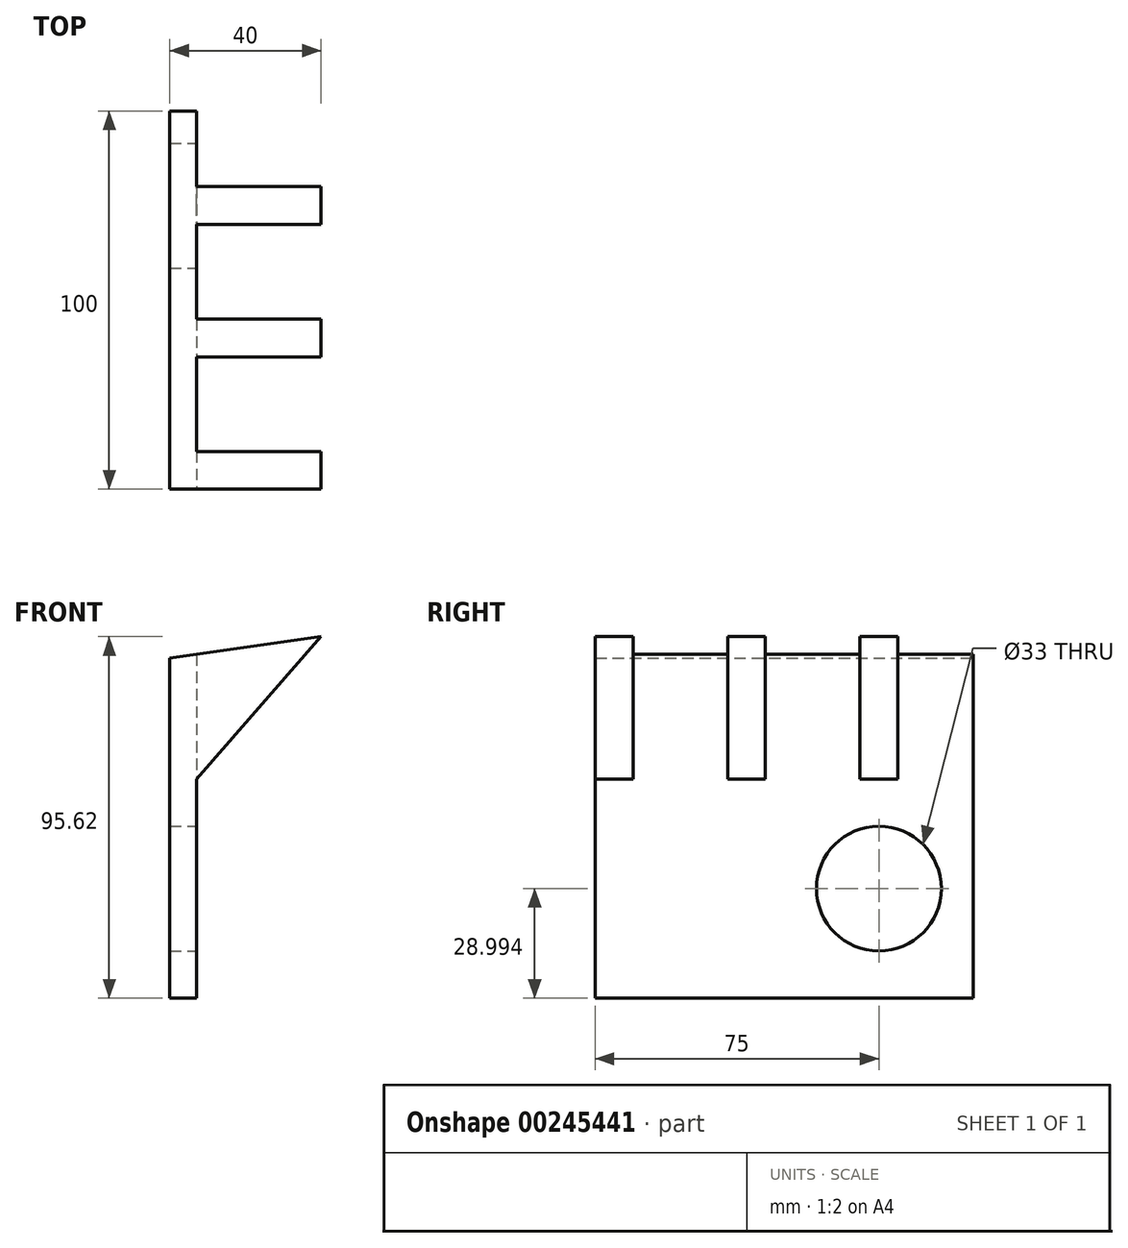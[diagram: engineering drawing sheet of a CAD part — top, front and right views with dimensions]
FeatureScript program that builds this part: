
annotation { "Feature Type Name" : "Feature", "Feature Type Description" : "" }
export const myFeature = defineFeature(function(context is Context, id is Id, definition is map)
    precondition{}
    {
        {
            var Q0;
            Q0=qCreatedBy(makeId("Front.planeOp"),FACE);
            var sketch = newSketch(context, id + "F0", { "sketchPlane" : qUnion([Q0])});
            skLineSegment(sketch, "E0", {"start": v(0, 0) * mm, "end": v(0, 90) * mm});
            skLineSegment(sketch, "E1", {"start": v(0, 90) * mm, "end": v(148.54, 110.88) * mm});
            skLineSegment(sketch, "E2", {"start": v(148.54, 110.88) * mm, "end": v(148.54, 0) * mm});
            skLineSegment(sketch, "E3", {"start": v(148.54, 0) * mm, "end": v(0, 0) * mm});
            skSolve(sketch);
        }
        {
            var Q0;
            Q0=qSketchRegion(id+"F0",true);
            extrude(context, id + "F1", {"entities" : qUnion([Q0]), "depth" : 100 * mm});
        }
        {
            var Q0;
            Q0=makeQuery(id+"F1.opExtrude","CAP_FACE",FACE,{"disambiguationData":[OSD([sQuery(id+"F0.wireOp",EDGE,"E0"),sQuery(id+"F0.wireOp",EDGE,"E1"),sQuery(id+"F0.wireOp",EDGE,"E2"),sQuery(id+"F0.wireOp",EDGE,"E3")])],"isStart":false});
            var sketch = newSketch(context, id + "F2", { "sketchPlane" : qUnion([Q0])});
            skLineSegment(sketch, "E4", {"start": v(0, 0) * mm, "end": v(7, 0) * mm});
            skLineSegment(sketch, "E5.bottom", {"start": v(40, 0) * mm, "end": v(148.54, 0) * mm});
            skLineSegment(sketch, "E5.top", {"start": v(40, 169.22) * mm, "end": v(148.54, 169.22) * mm});
            skLineSegment(sketch, "E5.left", {"start": v(40, 95.62) * mm, "end": v(40, 169.22) * mm});
            skLineSegment(sketch, "E5.right", {"start": v(148.54, 0) * mm, "end": v(148.54, 169.22) * mm});
            skLineSegment(sketch, "E6", {"start": v(40, 95.62) * mm, "end": v(7, 57.99) * mm});
            skLineSegment(sketch, "E7", {"start": v(7, 57.99) * mm, "end": v(7, 0) * mm});
            skLineSegment(sketch, "E8", {"start": v(7, 0) * mm, "end": v(40, 0) * mm});
            skSolve(sketch);
        }
        {
            var Q0;
            Q0=qSketchRegion(id+"F2",true);
            extrude(context, id + "F3", {"entities" : qUnion([Q0]), "operationType" : NewBodyOperationType.REMOVE, "oppositeDirection" : true, "depth" : 100 * mm});
        }
        {
            var Q0;
            Q0=makeQuery(id+"F1.opExtrude","SWEPT_FACE",FACE,{"disambiguationData":[OSD([sQuery(id+"F0.wireOp",EDGE,"E3")])]});
            var sketch = newSketch(context, id + "F4", { "sketchPlane" : qUnion([Q0])});
            skLineSegment(sketch, "E9", {"start": v(7, 100) * mm, "end": v(7, 90) * mm});
            skLineSegment(sketch, "E10.bottom", {"start": v(7, 90) * mm, "end": v(44.07, 90) * mm});
            skLineSegment(sketch, "E10.top", {"start": v(7, 65) * mm, "end": v(44.07, 65) * mm});
            skLineSegment(sketch, "E10.left", {"start": v(7, 90) * mm, "end": v(7, 65) * mm});
            skLineSegment(sketch, "E10.right", {"start": v(44.07, 90) * mm, "end": v(44.07, 65) * mm});
            skLineSegment(sketch, "E11", {"start": v(7, 65) * mm, "end": v(7, 55) * mm});
            skLineSegment(sketch, "E12.bottom", {"start": v(7, 55) * mm, "end": v(44.07, 55) * mm});
            skLineSegment(sketch, "E12.top", {"start": v(7, 30) * mm, "end": v(44.07, 30) * mm});
            skLineSegment(sketch, "E12.left", {"start": v(7, 55) * mm, "end": v(7, 30) * mm});
            skLineSegment(sketch, "E12.right", {"start": v(44.07, 55) * mm, "end": v(44.07, 30) * mm});
            skLineSegment(sketch, "E13", {"start": v(7, 30) * mm, "end": v(7, 20) * mm});
            skLineSegment(sketch, "E14.bottom", {"start": v(7, 20) * mm, "end": v(44.07, 20) * mm});
            skLineSegment(sketch, "E14.top", {"start": v(7, -3.26) * mm, "end": v(44.07, -3.26) * mm});
            skLineSegment(sketch, "E14.left", {"start": v(7, 20) * mm, "end": v(7, -3.26) * mm});
            skLineSegment(sketch, "E14.right", {"start": v(44.07, 20) * mm, "end": v(44.07, -3.26) * mm});
            skSolve(sketch);
        }
        {
            var Q0;
            Q0=qSketchRegion(id+"F4",true);
            extrude(context, id + "F5", {"entities" : qUnion([Q0]), "operationType" : NewBodyOperationType.REMOVE, "oppositeDirection" : true, "depth" : 150 * mm});
        }
        {
            var Q0;
            Q0=makeQuery(id+"F5.boolean.opBoolean","MERGE",FACE,{"derivedFrom":[makeQuery(id+"F3.boolean.opBoolean","COPY",FACE,{"derivedFrom":makeQuery(id+"F3.opExtrude","SWEPT_FACE",FACE,{"disambiguationData":[OSD([sQuery(id+"F2.wireOp",EDGE,"E7")])]})}),makeQuery(id+"F5.opExtrude","SWEPT_FACE",FACE,{"disambiguationData":[OSD([sQuery(id+"F4.wireOp",EDGE,"E10.left")])]}),makeQuery(id+"F5.opExtrude","SWEPT_FACE",FACE,{"disambiguationData":[OSD([sQuery(id+"F4.wireOp",EDGE,"E12.left")])]}),makeQuery(id+"F5.opExtrude","SWEPT_FACE",FACE,{"disambiguationData":[OSD([sQuery(id+"F4.wireOp",EDGE,"E14.left")])]})]});
            var sketch = newSketch(context, id + "F6", { "sketchPlane" : qUnion([Q0])});
            skPoint(sketch, "E15.endSnap0", {"position": v(0, 45.5) * mm});
            skLineSegment(sketch, "E16", {"start": v(-50, 0) * mm, "end": v(-50, 57.99) * mm});
            skLineSegment(sketch, "E17", {"start": v(-50, 29) * mm, "end": v(0, 29) * mm});
            skCircle(sketch, "E18", {"center": v(-25, 29) * mm, "radius": 16.5 * mm});
            skSolve(sketch);
        }
        {
            var Q0;
            Q0=qSketchRegion(id+"F6",true);
            extrude(context, id + "F7", {"entities" : qUnion([Q0]), "operationType" : NewBodyOperationType.REMOVE, "oppositeDirection" : true, "depth" : 25 * mm});
        }
    });
